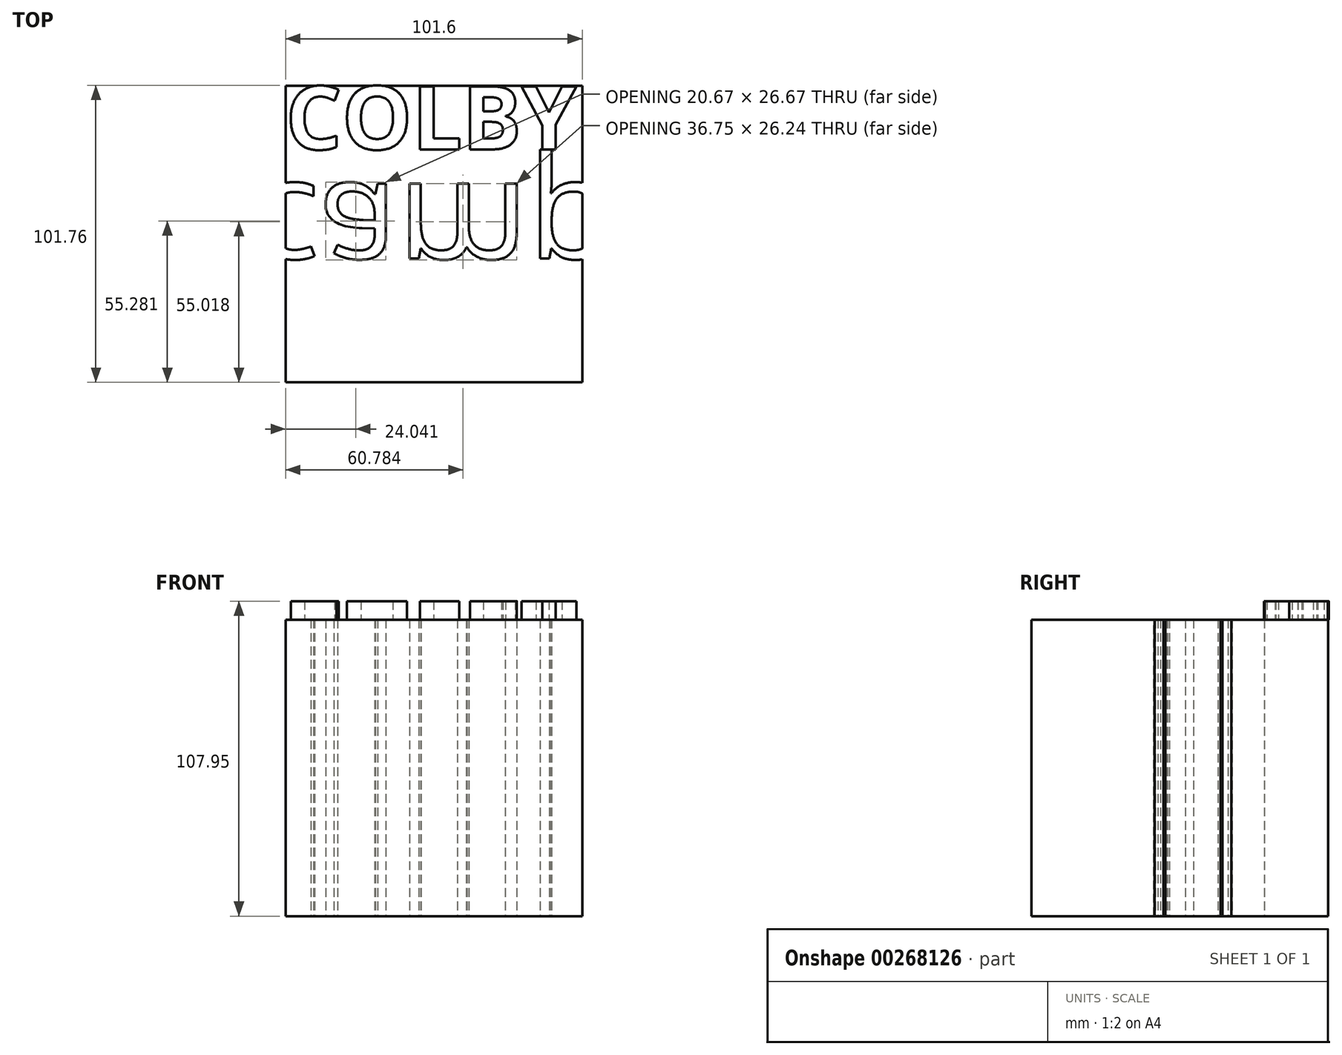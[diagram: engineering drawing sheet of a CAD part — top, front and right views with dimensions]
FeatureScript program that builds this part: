
annotation { "Feature Type Name" : "Feature", "Feature Type Description" : "" }
export const myFeature = defineFeature(function(context is Context, id is Id, definition is map)
    precondition{}
    {
        {
            var Q0;
            Q0=qCreatedBy(makeId("Front.planeOp"),FACE);
            var sketch = newSketch(context, id + "F0", { "sketchPlane" : qUnion([Q0])});
            skLineSegment(sketch, "E0.bottom", {"start": v(50.8, 50.8) * mm, "end": v(-50.8, 50.8) * mm});
            skLineSegment(sketch, "E0.top", {"start": v(50.8, -50.8) * mm, "end": v(-50.8, -50.8) * mm});
            skLineSegment(sketch, "E0.left", {"start": v(50.8, 50.8) * mm, "end": v(50.8, -50.8) * mm});
            skLineSegment(sketch, "E0.right", {"start": v(-50.8, 50.8) * mm, "end": v(-50.8, -50.8) * mm});
            skPoint(sketch, "E0.middle", {"position": v(0, 0) * mm});
            skSolve(sketch);
        }
        {
            var Q0;
            Q0 = qSketchRegion(id + "F0", true);
            extrude(context, id + "F1", {"entities" : qUnion([Q0]), "endBound" : BoundingType.SYMMETRIC, "depth" : 101.6 * mm});
        }
        {
            var Q0;
            Q0=makeQuery(id+"F1.opExtrude","SWEPT_FACE",FACE,{"disambiguationData":[OSD([sQuery(id+"F0.wireOp",EDGE,"E0.bottom")])]});
            var sketch = newSketch(context, id + "F2", { "sketchPlane" : qUnion([Q0])});
            skText(sketch, "E1", { "text": "COLBY", "fontName": "OpenSans-Bold.ttf"});
            const initialGuessF2  = {"E1": [-0.0508, 0.02902, 1, 0, 0.02178]};
            skSetInitialGuess(sketch, initialGuessF2);
            skSolve(sketch);
        }
        {
            var Q0;
            Q0 = qSketchRegion(id + "F2", true);
            extrude(context, id + "F3", {"entities" : qUnion([Q0]), "operationType" : NewBodyOperationType.ADD, "depth" : 6.35 * mm});
        }
        {
            var Q0;
            Q0=makeQuery(id+"F1.opExtrude","SWEPT_FACE",FACE,{"disambiguationData":[OSD([sQuery(id+"F0.wireOp",EDGE,"E0.top")])]});
            var sketch = newSketch(context, id + "F4", { "sketchPlane" : qUnion([Q0])});
            skText(sketch, "E2", { "text": "camp", "fontName": "OpenSans-Regular.ttf"});
            skLineSegment(sketch, "E3", {"start": v(-62.23, 17.34) * mm, "end": v(0, 0) * mm, "construction": true});
            skLineSegment(sketch, "E4", {"start": v(0, 0) * mm, "end": v(62.23, 17.34) * mm, "construction": true});
            skLineSegment(sketch, "E5", {"start": v(-62.23, -17.34) * mm, "end": v(0, 0) * mm, "construction": true});
            const initialGuessF4  = {"E2": [-0.06223, -0.01734, 1, 0, 0.03467]};
            skSetInitialGuess(sketch, initialGuessF4);
            skSolve(sketch);
        }
        {
            var Q0;
            Q0 = qSketchRegion(id + "F4", true);
            extrude(context, id + "F5", {"entities" : qUnion([Q0]), "operationType" : NewBodyOperationType.REMOVE, "oppositeDirection" : true, "depth" : 121.67 * mm});
        }
    });
